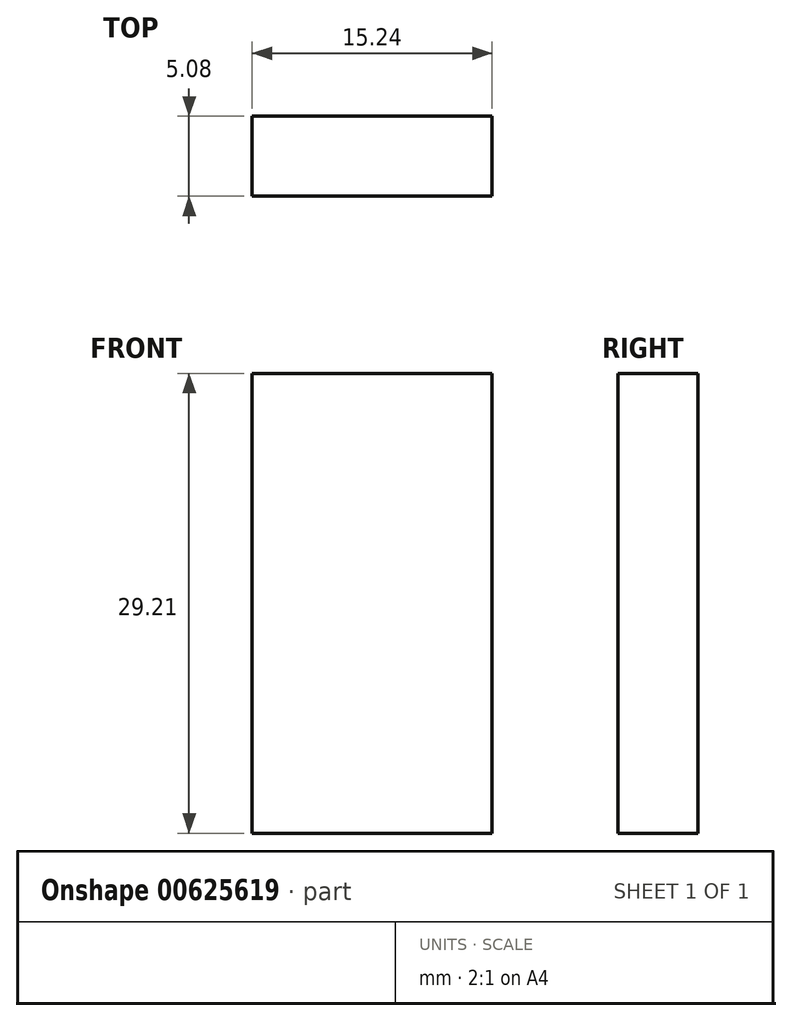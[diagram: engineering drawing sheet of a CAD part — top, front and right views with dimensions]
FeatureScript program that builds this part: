
annotation { "Feature Type Name" : "Feature", "Feature Type Description" : "" }
export const myFeature = defineFeature(function(context is Context, id is Id, definition is map)
    precondition{}
    {
        {
            var Q0;
            Q0=qCreatedBy(makeId("Top.planeOp"),FACE);
            var sketch = newSketch(context, id + "F0", { "sketchPlane" : qUnion([Q0])});
            skLineSegment(sketch, "E0.bottom", {"start": v(0, 0) * mm, "end": v(15.24, 0) * mm});
            skLineSegment(sketch, "E0.top", {"start": v(0, -5.08) * mm, "end": v(15.24, -5.08) * mm});
            skLineSegment(sketch, "E0.left", {"start": v(0, 0) * mm, "end": v(0, -5.08) * mm});
            skLineSegment(sketch, "E0.right", {"start": v(15.24, 0) * mm, "end": v(15.24, -5.08) * mm});
            skSolve(sketch);
        }
        {
            var Q0;
            Q0=makeQuery(id+"F0.imprint","IMPRINT",FACE,{"disambiguationData":[TD([[makeQuery(id+"F0.imprint","IMPRINT",EDGE,{"derivedFrom":sQuery(id+"F0.wireOp",EDGE,"E0.bottom")}),-1.0]])]});
            extrude(context, id + "F1", {"entities" : qUnion([Q0]), "depth" : 29.2 * mm, "offsetDistance" : 25.4 * mm});
        }
    });
